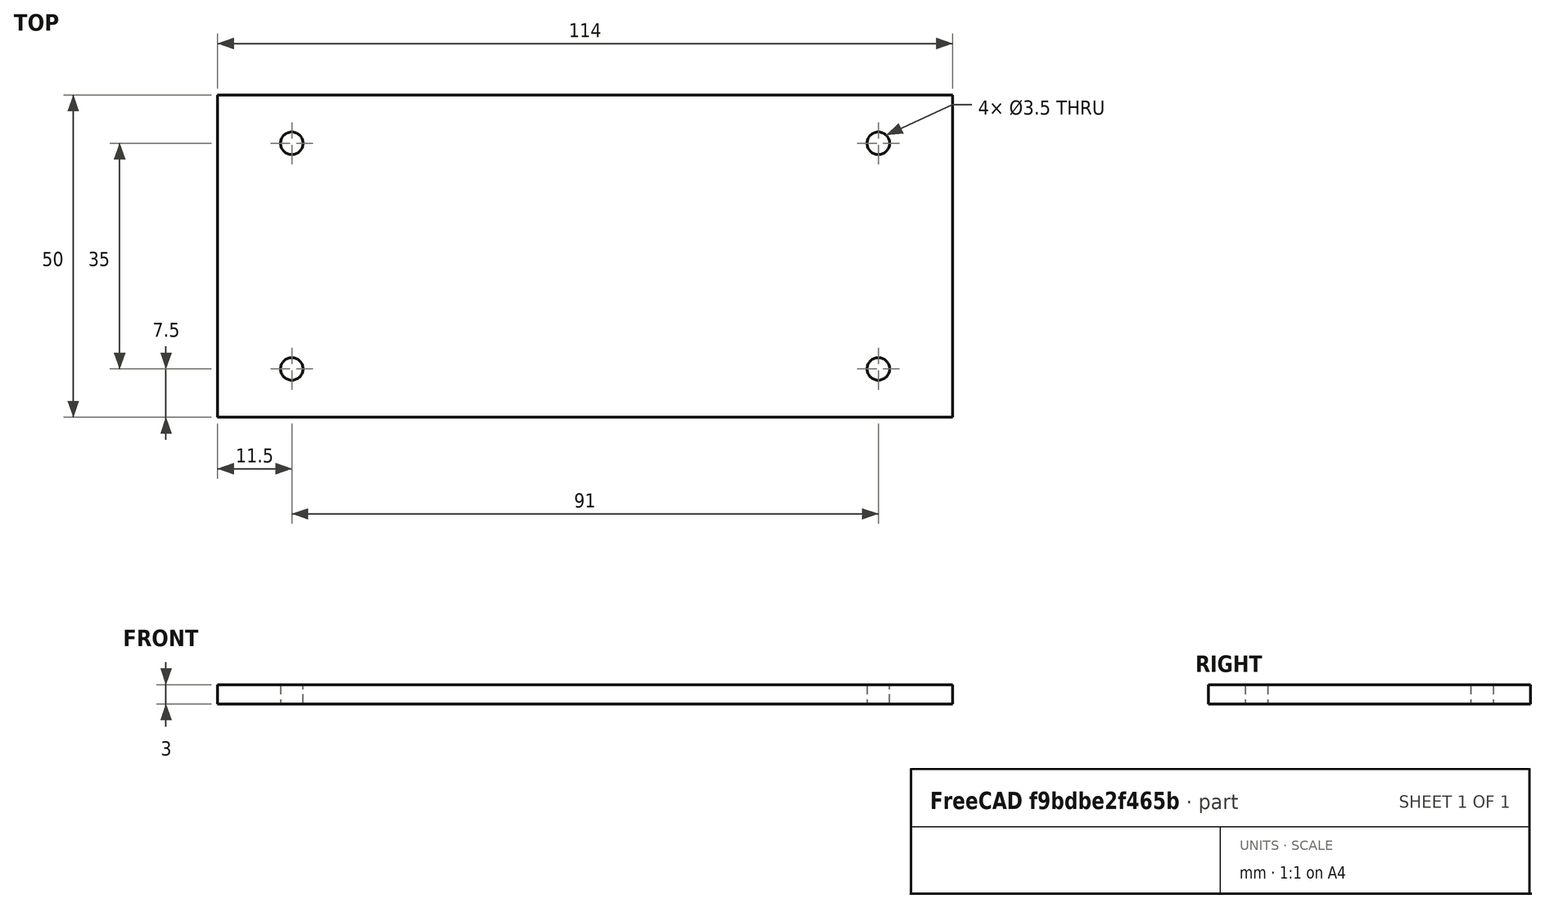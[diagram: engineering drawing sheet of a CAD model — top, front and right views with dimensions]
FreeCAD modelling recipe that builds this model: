
FCSTD DOCUMENT  (FreeCAD 0.17R13541 (Git))
Label: AB_boards-support-plate
License: All rights reserved
LicenseURL: http://en.wikipedia.org/wiki/All_rights_reserved
objects: Sketcher::SketchObject×1, PartDesign::Pad×1, PartDesign::Body×1
note: 4 computed .brp shape members not serialized (recipe doc carries the construction recipe); baked Part::Feature solids carry a one-line shape summary decoded from their .brp

FEATURE [Sketcher::SketchObject] Sketch
  MapMode = 5
  Support = -> [XY_Plane]
  sketch-geometry (8):
    g0: Circle CenterX=-45.5 CenterY=17.5 CenterZ=0 NormalX=0 NormalY=0 NormalZ=1 AngleXU=0 Radius=1.75
    g1: Circle CenterX=-45.5 CenterY=-17.5 CenterZ=0 NormalX=0 NormalY=0 NormalZ=1 AngleXU=0 Radius=1.75
    g2: Circle CenterX=45.5 CenterY=-17.5 CenterZ=0 NormalX=0 NormalY=0 NormalZ=1 AngleXU=0 Radius=1.75
    g3: Circle CenterX=45.5 CenterY=17.5 CenterZ=0 NormalX=0 NormalY=0 NormalZ=1 AngleXU=0 Radius=1.75
    g4: LineSegment StartX=-57 StartY=25 StartZ=0 EndX=57 EndY=25 EndZ=0
    g5: LineSegment StartX=57 StartY=25 StartZ=0 EndX=57 EndY=-25 EndZ=0
    g6: LineSegment StartX=57 StartY=-25 StartZ=0 EndX=-57 EndY=-25 EndZ=0
    g7: LineSegment StartX=-57 StartY=-25 StartZ=0 EndX=-57 EndY=25 EndZ=0
  constraints (21):
    c: Equal(g0,g1)
    c: Equal(g1,g2)
    c: Equal(g2,g3)
    c: Radius(g0) = 1.75
    c: Coincident(g4,g5)
    c: Coincident(g5,g6)
    c: Coincident(g6,g7)
    c: Coincident(g7,g4)
    c: Horizontal(g4)
    c: Horizontal(g6)
    c: Vertical(g5)
    c: Vertical(g7)
    c: DistanceX(g4,g4) = 114
    c: DistanceY(g7,g7) = 50
    c: DistanceX(g6,g-1) = 57
    c: DistanceY(g6,g-1) = 25
    c: Symmetric(g3,g0,g-2)
    c: Symmetric(g3,g2,g-1)
    c: Symmetric(g1,g2,g-2)
    c: DistanceY(g1,g0) = 35
    c: DistanceX(g0,g3) = 91
FEATURE [PartDesign::Pad] Pad
  Length = 3
  Length2 = 100
  Profile = -> Sketch
  Type = 0
FEATURE [PartDesign::Body] Body
  Group = -> [Sketch,Pad]
  Origin = -> Origin
  Tip = -> Pad
